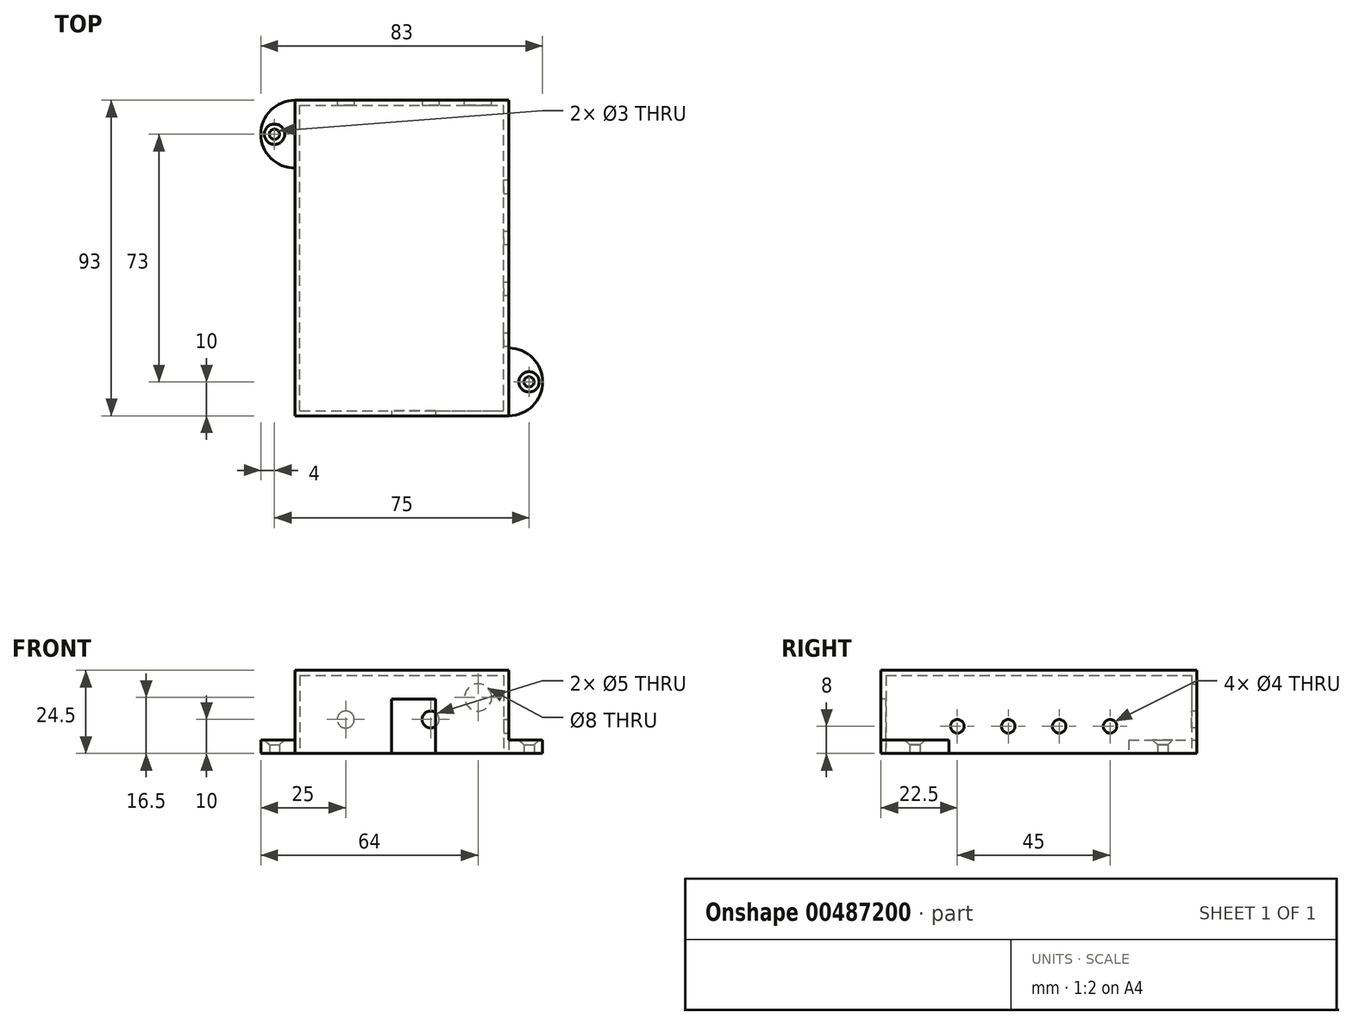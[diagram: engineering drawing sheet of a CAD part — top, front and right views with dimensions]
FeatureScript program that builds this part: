
annotation { "Feature Type Name" : "Feature", "Feature Type Description" : "" }
export const myFeature = defineFeature(function(context is Context, id is Id, definition is map)
    precondition{}
    {
        {
            var Q0;
            Q0=qCreatedBy(makeId("Top.planeOp"),FACE);
            var sketch = newSketch(context, id + "F0", { "sketchPlane" : qUnion([Q0])});
            skLineSegment(sketch, "E0.bottom", {"start": v(0, 0) * mm, "end": v(60, 0) * mm});
            skLineSegment(sketch, "E0.top", {"start": v(0, 90) * mm, "end": v(60, 90) * mm});
            skLineSegment(sketch, "E0.left", {"start": v(0, 0) * mm, "end": v(0, 90) * mm});
            skLineSegment(sketch, "E0.right", {"start": v(60, 0) * mm, "end": v(60, 90) * mm});
            skLineSegment(sketch, "E1.bottom", {"start": v(-1.5, -1.5) * mm, "end": v(61.5, -1.5) * mm});
            skLineSegment(sketch, "E1.top", {"start": v(-1.5, 91.5) * mm, "end": v(61.5, 91.5) * mm});
            skLineSegment(sketch, "E1.left", {"start": v(-1.5, -1.5) * mm, "end": v(-1.5, 91.5) * mm});
            skLineSegment(sketch, "E1.right", {"start": v(61.5, -1.5) * mm, "end": v(61.5, 91.5) * mm});
            skSolve(sketch);
        }
        {
            var Q0;
            Q0 = qSketchRegion(id + "F0", true);
            var Q1;
            Q1 = qSketchRegion(id + "F8", true);
            extrude(context, id + "F1", {"entities" : qUnion([Q0, Q1]), "depth" : 23 * mm});
        }
        {
            var Q0;
            Q0=makeQuery(id+"F1.opExtrude","SWEPT_FACE",FACE,{"disambiguationData":[OSD([sQuery(id+"F0.wireOp",EDGE,"E1.bottom")])]});
            var sketch = newSketch(context, id + "F2", { "sketchPlane" : qUnion([Q0])});
            skLineSegment(sketch, "E2.bottom", {"start": v(27, 16) * mm, "end": v(40, 16) * mm});
            skLineSegment(sketch, "E2.top", {"start": v(27, 0) * mm, "end": v(40, 0) * mm});
            skLineSegment(sketch, "E2.left", {"start": v(27, 16) * mm, "end": v(27, 0) * mm});
            skLineSegment(sketch, "E2.right", {"start": v(40, 16) * mm, "end": v(40, 0) * mm});
            skSolve(sketch);
        }
        {
            var Q0;
            Q0=makeQuery(id+"F2.imprint","IMPRINT",FACE,{"disambiguationData":[TD([[makeQuery(id+"F2.imprint","IMPRINT",EDGE,{"derivedFrom":sQuery(id+"F2.wireOp",EDGE,"E2.bottom")}),-1.0]])]});
            extrude(context, id + "F3", {"entities" : qUnion([Q0]), "operationType" : NewBodyOperationType.REMOVE, "oppositeDirection" : true, "depth" : 25 * mm});
        }
        {
            var Q0;
            Q0=makeQuery(id+"F1.opExtrude","SWEPT_FACE",FACE,{"disambiguationData":[OSD([sQuery(id+"F0.wireOp",EDGE,"E1.right")])]});
            var sketch = newSketch(context, id + "F4", { "sketchPlane" : qUnion([Q0])});
            skPoint(sketch, "E3", {"position": v(21, 8) * mm});
            skPoint(sketch, "E4", {"position": v(36, 8) * mm});
            skPoint(sketch, "E5", {"position": v(66, 8) * mm});
            skLineSegment(sketch, "E6", {"start": v(66, 8) * mm, "end": v(21, 8) * mm, "construction": true});
            skPoint(sketch, "E7", {"position": v(51, 8) * mm});
            skSolve(sketch);
        }
        {
            var Q0;
            Q0=sQuery(id+"F4.wireOp",VERTEX,"E7");
            var Q1;
            Q1=sQuery(id+"F4.wireOp",VERTEX,"E5");
            var Q2;
            Q2=sQuery(id+"F4.wireOp",VERTEX,"E4");
            var Q3;
            Q3=sQuery(id+"F4.wireOp",VERTEX,"E3");
            var Q4;
            Q4=makeQuery(id+"F1.opExtrude","SWEPT_BODY",BODY,{"disambiguationData":[OSD([sQuery(id+"F0.wireOp",EDGE,"E0.bottom"),sQuery(id+"F0.wireOp",EDGE,"E0.top"),sQuery(id+"F0.wireOp",EDGE,"E0.left"),sQuery(id+"F0.wireOp",EDGE,"E0.right"),sQuery(id+"F0.wireOp",EDGE,"E1.bottom"),sQuery(id+"F0.wireOp",EDGE,"E1.top"),sQuery(id+"F0.wireOp",EDGE,"E1.left"),sQuery(id+"F0.wireOp",EDGE,"E1.right")])]});
            hole(context, id + "F5", {"style" : HoleStyle.SIMPLE, "endStyle" : HoleEndStyle.BLIND, "holeDiameter" : 4 * mm, "holeDepth" : 12 * mm, "isTappedThrough" : true, "tappedDepth" : 12 * mm, "tapClearance" : 3, "locations" : qUnion([Q0, Q1, Q2, Q3]), "scope" : qUnion([Q4])});
        }
        {
            var Q0;
            Q0=makeQuery(id+"F1.opExtrude","SWEPT_FACE",FACE,{"disambiguationData":[OSD([sQuery(id+"F0.wireOp",EDGE,"E0.top")])]});
            var sketch = newSketch(context, id + "F6", { "sketchPlane" : qUnion([Q0])});
            skLineSegment(sketch, "E8", {"start": v(38.5, 10) * mm, "end": v(13.5, 10) * mm, "construction": true});
            skSolve(sketch);
        }
        {
            var Q0;
            Q0=sQuery(id+"F6.wireOp",VERTEX,"E8.end");
            var Q1;
            Q1=sQuery(id+"F6.wireOp",VERTEX,"E8.start");
            var Q2;
            Q2=makeQuery(id+"F1.opExtrude","SWEPT_BODY",BODY,{"disambiguationData":[OSD([sQuery(id+"F0.wireOp",EDGE,"E0.bottom"),sQuery(id+"F0.wireOp",EDGE,"E0.top"),sQuery(id+"F0.wireOp",EDGE,"E0.left"),sQuery(id+"F0.wireOp",EDGE,"E0.right"),sQuery(id+"F0.wireOp",EDGE,"E1.bottom"),sQuery(id+"F0.wireOp",EDGE,"E1.top"),sQuery(id+"F0.wireOp",EDGE,"E1.left"),sQuery(id+"F0.wireOp",EDGE,"E1.right")])]});
            hole(context, id + "F7", {"style" : HoleStyle.SIMPLE, "endStyle" : HoleEndStyle.BLIND, "holeDiameter" : 5 * mm, "holeDepth" : 12 * mm, "isTappedThrough" : true, "tappedDepth" : 12 * mm, "tapClearance" : 3, "locations" : qUnion([Q0, Q1]), "scope" : qUnion([Q2])});
        }
        {
            var Q0;
            Q0=makeQuery(id+"F1.opExtrude","SWEPT_FACE",FACE,{"disambiguationData":[OSD([sQuery(id+"F0.wireOp",EDGE,"E1.top")])]});
            var sketch = newSketch(context, id + "F8", { "sketchPlane" : qUnion([Q0])});
            skPoint(sketch, "E9", {"position": v(-52.5, 16.5) * mm});
            skSolve(sketch);
        }
        {
            var Q0;
            Q0=sQuery(id+"F8.wireOp",VERTEX,"E9");
            var Q1;
            Q1=makeQuery(id+"F1.opExtrude","SWEPT_BODY",BODY,{"disambiguationData":[OSD([sQuery(id+"F0.wireOp",EDGE,"E0.bottom"),sQuery(id+"F0.wireOp",EDGE,"E0.top"),sQuery(id+"F0.wireOp",EDGE,"E0.left"),sQuery(id+"F0.wireOp",EDGE,"E0.right"),sQuery(id+"F0.wireOp",EDGE,"E1.bottom"),sQuery(id+"F0.wireOp",EDGE,"E1.top"),sQuery(id+"F0.wireOp",EDGE,"E1.left"),sQuery(id+"F0.wireOp",EDGE,"E1.right")])]});
            hole(context, id + "F9", {"style" : HoleStyle.SIMPLE, "endStyle" : HoleEndStyle.BLIND, "holeDiameter" : 8 * mm, "holeDepth" : 12 * mm, "isTappedThrough" : true, "tappedDepth" : 12 * mm, "tapClearance" : 3, "locations" : qUnion([Q0]), "scope" : qUnion([Q1])});
        }
        {
            var Q0;
            Q0=makeQuery(id+"F1.opExtrude","CAP_FACE",FACE,{"disambiguationData":[OSD([sQuery(id+"F0.wireOp",EDGE,"E0.bottom"),sQuery(id+"F0.wireOp",EDGE,"E0.top"),sQuery(id+"F0.wireOp",EDGE,"E0.left"),sQuery(id+"F0.wireOp",EDGE,"E0.right"),sQuery(id+"F0.wireOp",EDGE,"E1.bottom"),sQuery(id+"F0.wireOp",EDGE,"E1.top"),sQuery(id+"F0.wireOp",EDGE,"E1.left"),sQuery(id+"F0.wireOp",EDGE,"E1.right")])],"isStart":false});
            var sketch = newSketch(context, id + "F10", { "sketchPlane" : qUnion([Q0])});
            skLineSegment(sketch, "E10.bottom", {"start": v(-1.5, -1.5) * mm, "end": v(61.5, -1.5) * mm});
            skLineSegment(sketch, "E10.top", {"start": v(-1.5, 91.5) * mm, "end": v(61.5, 91.5) * mm});
            skLineSegment(sketch, "E10.left", {"start": v(-1.5, -1.5) * mm, "end": v(-1.5, 91.5) * mm});
            skLineSegment(sketch, "E10.right", {"start": v(61.5, -1.5) * mm, "end": v(61.5, 91.5) * mm});
            skSolve(sketch);
        }
        {
            var Q0;
            Q0 = qSketchRegion(id + "F10", true);
            extrude(context, id + "F11", {"entities" : qUnion([Q0]), "operationType" : NewBodyOperationType.ADD, "depth" : 1.5 * mm});
        }
        {
            var Q0;
            Q0=makeQuery(id+"F1.opExtrude","CAP_FACE",FACE,{"disambiguationData":[OSD([sQuery(id+"F0.wireOp",EDGE,"E0.bottom"),sQuery(id+"F0.wireOp",EDGE,"E0.top"),sQuery(id+"F0.wireOp",EDGE,"E0.left"),sQuery(id+"F0.wireOp",EDGE,"E0.right"),sQuery(id+"F0.wireOp",EDGE,"E1.bottom"),sQuery(id+"F0.wireOp",EDGE,"E1.top"),sQuery(id+"F0.wireOp",EDGE,"E1.left"),sQuery(id+"F0.wireOp",EDGE,"E1.right")])],"isStart":true});
            var sketch = newSketch(context, id + "F12", { "sketchPlane" : qUnion([Q0])});
            skArc(sketch, "E11", {"start": v(61.5, -18.5) * mm, "mid": v(71.5, -8.5) * mm, "end": v(61.5, 1.5) * mm});
            skArc(sketch, "E12", {"start": v(-1.5, -71.5) * mm, "mid": v(-11.5, -81.5) * mm, "end": v(-1.5, -91.5) * mm});
            skCircle(sketch, "E13", {"center": v(67.5, -8.5) * mm, "radius": 1.5 * mm});
            skCircle(sketch, "E14", {"center": v(-7.5, -81.5) * mm, "radius": 1.5 * mm});
            skLineSegment(sketch, "E15", {"start": v(61.5, 1.5) * mm, "end": v(61.5, -18.5) * mm});
            skLineSegment(sketch, "E16", {"start": v(-1.5, -71.5) * mm, "end": v(-1.5, -91.5) * mm});
            skSolve(sketch);
        }
        {
            var Q0;
            {var subQ0=sQuery(id+"F12.wireOp",EDGE,"E12");Q0=makeQuery(id+"F12.imprint","IMPRINT",FACE,{"disambiguationData":[TD([[makeQuery(id+"F12.imprint","IMPRINT",EDGE,{"derivedFrom":subQ0}),1.0]])]});}
            var Q1;
            {var subQ0=sQuery(id+"F12.wireOp",EDGE,"E11");Q1=makeQuery(id+"F12.imprint","IMPRINT",FACE,{"disambiguationData":[TD([[makeQuery(id+"F12.imprint","IMPRINT",EDGE,{"derivedFrom":subQ0}),1.0]])]});}
            extrude(context, id + "F13", {"entities" : qUnion([Q0, Q1]), "operationType" : NewBodyOperationType.ADD, "depth" : -4 * mm});
        }
        {
            var Q0;
            Q0=makeQuery(id+"F13.opExtrude","CAP_EDGE",EDGE,{"disambiguationData":[OSD([sQuery(id+"F12.wireOp",EDGE,"E14")])],"isStart":false});
            var Q1;
            Q1=makeQuery(id+"F13.opExtrude","CAP_EDGE",EDGE,{"disambiguationData":[OSD([sQuery(id+"F12.wireOp",EDGE,"E13")])],"isStart":false});
            chamfer(context, id + "F14", {"entities" : qUnion([Q0, Q1]), "width" : 1.5 * mm, "tangentPropagation" : true});
        }
    });
